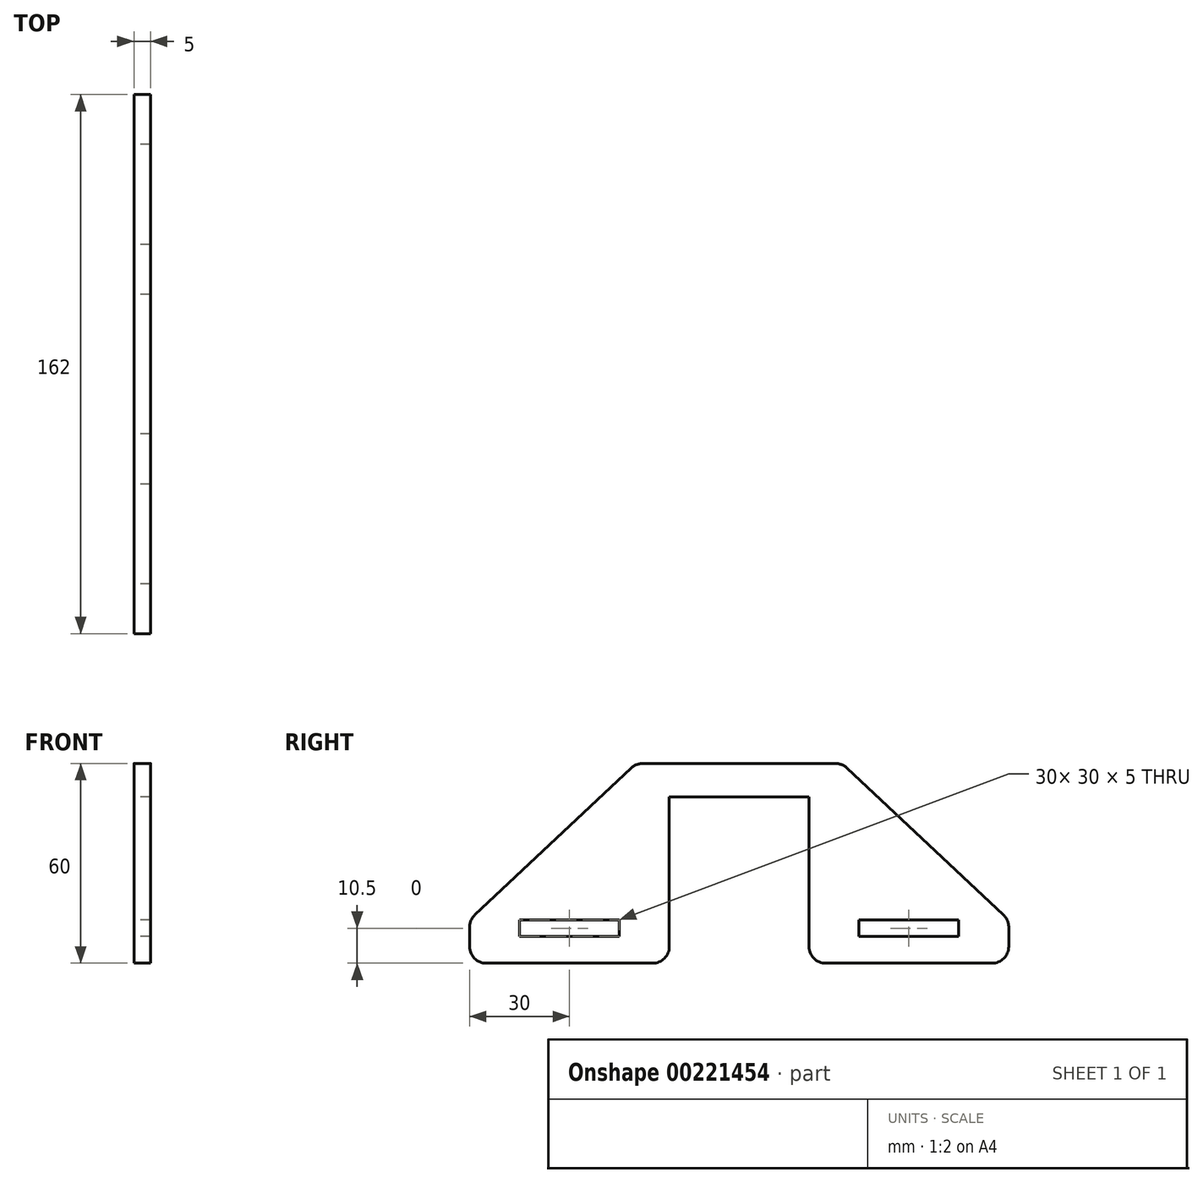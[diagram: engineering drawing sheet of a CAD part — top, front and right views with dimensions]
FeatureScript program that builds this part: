
annotation { "Feature Type Name" : "Feature", "Feature Type Description" : "" }
export const myFeature = defineFeature(function(context is Context, id is Id, definition is map)
    precondition{}
    {
        {
            var Q0;
            Q0=qCreatedBy(makeId("Right.planeOp"),FACE);
            var sketch = newSketch(context, id + "F0", { "sketchPlane" : qUnion([Q0])});
            skLineSegment(sketch, "E0", {"start": v(0, 5) * mm, "end": v(0, 50) * mm});
            skLineSegment(sketch, "E1", {"start": v(0, 50) * mm, "end": v(42, 50) * mm});
            skLineSegment(sketch, "E2", {"start": v(42, 50) * mm, "end": v(42, 5) * mm});
            skLineSegment(sketch, "E3", {"start": v(-5, 0) * mm, "end": v(-55, 0) * mm});
            skLineSegment(sketch, "E4", {"start": v(-60, 5) * mm, "end": v(-60, 10.84) * mm});
            skLineSegment(sketch, "E5", {"start": v(-60, 8) * mm, "end": v(0, 8) * mm, "construction": true});
            skLineSegment(sketch, "E6.bottom", {"start": v(-45, 8) * mm, "end": v(-15, 8) * mm});
            skLineSegment(sketch, "E6.top", {"start": v(-45, 13) * mm, "end": v(-15, 13) * mm});
            skLineSegment(sketch, "E6.left", {"start": v(-45, 8) * mm, "end": v(-45, 13) * mm});
            skLineSegment(sketch, "E6.right", {"start": v(-15, 8) * mm, "end": v(-15, 13) * mm});
            skPoint(sketch, "E7", {"position": v(-30, 8) * mm});
            skPoint(sketch, "E8", {"position": v(-30, 0) * mm});
            skLineSegment(sketch, "E9", {"start": v(-8.02, 60) * mm, "end": v(50.02, 60) * mm});
            skLineSegment(sketch, "E10", {"start": v(-58.42, 14.48) * mm, "end": v(-11.44, 58.64) * mm});
            skPoint(sketch, "E11.visualSharp", {"position": v(-10, 60) * mm});
            skArc(sketch, "E11.filletArc", {"start": v(-8.02, 60) * mm, "mid": v(-9.86, 59.65) * mm, "end": v(-11.44, 58.64) * mm});
            skLineSegment(sketch, "E12", {"start": v(21, 50) * mm, "end": v(21, 0) * mm, "construction": true});
            skLineSegment(sketch, "E13.MirrorCS", {"start": v(100.42, 14.48) * mm, "end": v(53.44, 58.64) * mm});
            skArc(sketch, "E14.MirrorCS", {"start": v(50.02, 60) * mm, "mid": v(51.86, 59.65) * mm, "end": v(53.44, 58.64) * mm});
            skLineSegment(sketch, "E15.MirrorCS", {"start": v(102, 5) * mm, "end": v(102, 10.84) * mm});
            skLineSegment(sketch, "E16.MirrorCS", {"start": v(47, 0) * mm, "end": v(97, 0) * mm});
            skLineSegment(sketch, "E17.MirrorCS", {"start": v(57, 8) * mm, "end": v(57, 13) * mm});
            skLineSegment(sketch, "E18.MirrorCS", {"start": v(87, 13) * mm, "end": v(57, 13) * mm});
            skLineSegment(sketch, "E19.MirrorCS", {"start": v(87, 8) * mm, "end": v(87, 13) * mm});
            skPoint(sketch, "E20.MirrorP", {"position": v(72, 8) * mm});
            skLineSegment(sketch, "E21.MirrorCS", {"start": v(87, 8) * mm, "end": v(57, 8) * mm});
            skPoint(sketch, "E22.visualSharp", {"position": v(0, 0) * mm});
            skArc(sketch, "E22.filletArc", {"start": v(-5, 0) * mm, "mid": v(-1.46, 1.46) * mm, "end": v(0, 5) * mm});
            skPoint(sketch, "E23.visualSharp", {"position": v(-60, 0) * mm});
            skArc(sketch, "E23.filletArc", {"start": v(-60, 5) * mm, "mid": v(-58.54, 1.46) * mm, "end": v(-55, 0) * mm});
            skPoint(sketch, "E24.visualSharp", {"position": v(42, 0) * mm});
            skArc(sketch, "E24.filletArc", {"start": v(42, 5) * mm, "mid": v(43.46, 1.46) * mm, "end": v(47, 0) * mm});
            skPoint(sketch, "E25.visualSharp", {"position": v(102, 0) * mm});
            skArc(sketch, "E25.filletArc", {"start": v(97, 0) * mm, "mid": v(100.54, 1.46) * mm, "end": v(102, 5) * mm});
            skPoint(sketch, "E26.visualSharp", {"position": v(-60, 13) * mm});
            skArc(sketch, "E26.filletArc", {"start": v(-58.42, 14.48) * mm, "mid": v(-59.59, 12.82) * mm, "end": v(-60, 10.84) * mm});
            skPoint(sketch, "E27.visualSharp", {"position": v(102, 13) * mm});
            skArc(sketch, "E27.filletArc", {"start": v(102, 10.84) * mm, "mid": v(101.59, 12.82) * mm, "end": v(100.42, 14.48) * mm});
            skSolve(sketch);
        }
        {
            var Q0;
            Q0 = qSketchRegion(id + "F0", true);
            extrude(context, id + "F1", {"entities" : qUnion([Q0]), "depth" : 5 * mm});
        }
    });
